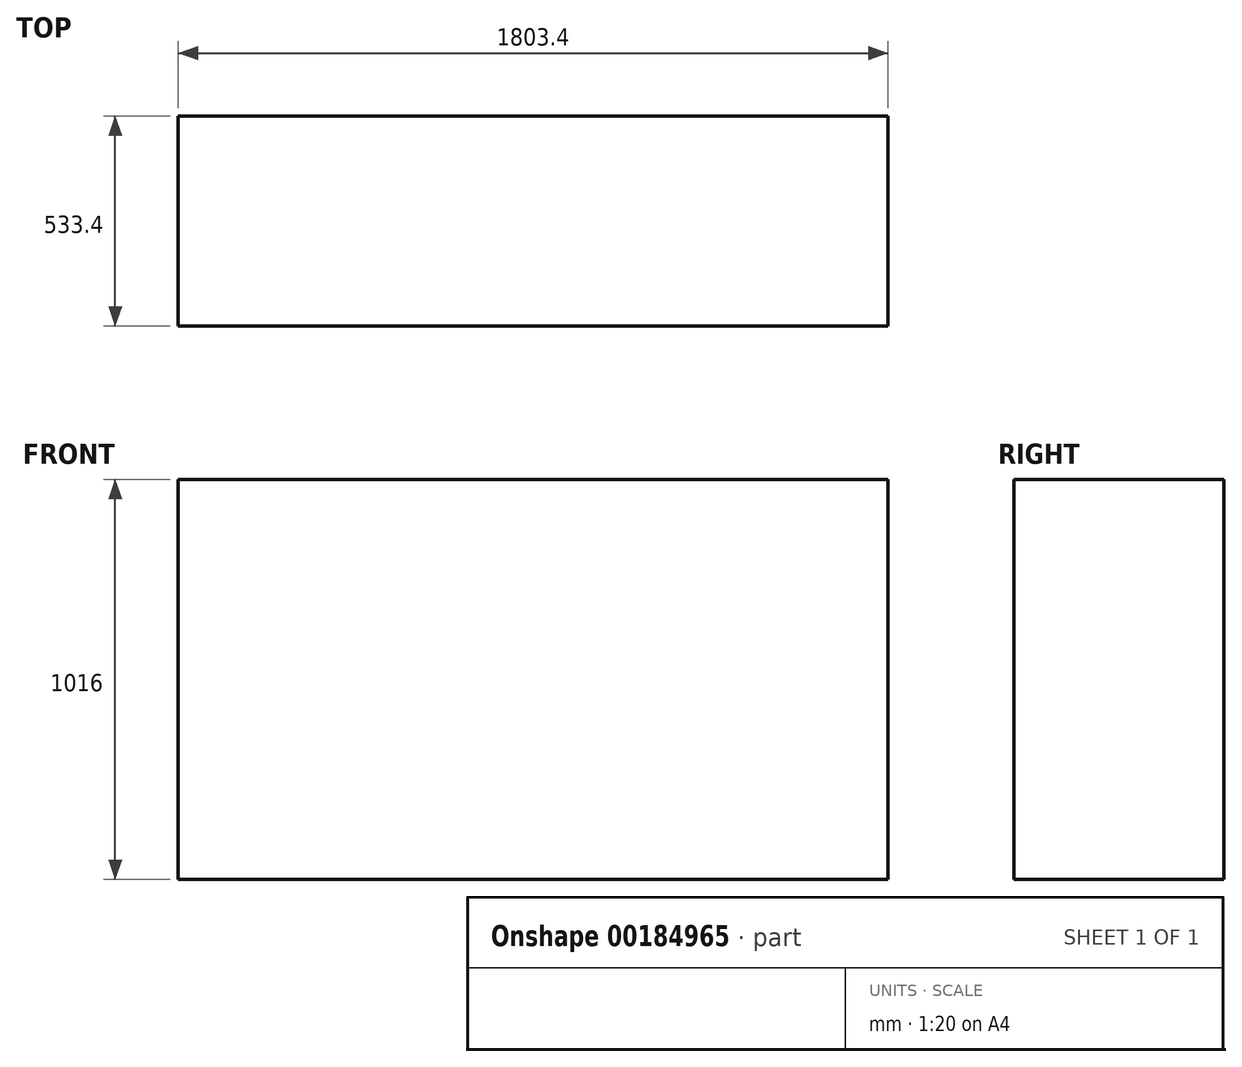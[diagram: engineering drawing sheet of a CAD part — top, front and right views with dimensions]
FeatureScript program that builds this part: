
annotation { "Feature Type Name" : "Feature", "Feature Type Description" : "" }
export const myFeature = defineFeature(function(context is Context, id is Id, definition is map)
    precondition{}
    {
        {
            var Q0;
            Q0=qCreatedBy(makeId("Top.planeOp"),FACE);
            var sketch = newSketch(context, id + "F0", { "sketchPlane" : qUnion([Q0])});
            skLineSegment(sketch, "E0.bottom", {"start": v(901.7, 266.7) * mm, "end": v(-901.7, 266.7) * mm});
            skLineSegment(sketch, "E0.top", {"start": v(901.7, -266.7) * mm, "end": v(-901.7, -266.7) * mm});
            skLineSegment(sketch, "E0.left", {"start": v(901.7, 266.7) * mm, "end": v(901.7, -266.7) * mm});
            skLineSegment(sketch, "E0.right", {"start": v(-901.7, 266.7) * mm, "end": v(-901.7, -266.7) * mm});
            skPoint(sketch, "E0.middle", {"position": v(0, 0) * mm});
            skSolve(sketch);
        }
        {
            var Q0;
            Q0=makeQuery(id+"F0.imprint","IMPRINT",FACE,{"disambiguationData":[TD([[makeQuery(id+"F0.imprint","IMPRINT",EDGE,{"derivedFrom":sQuery(id+"F0.wireOp",EDGE,"E0.bottom")}),1.0]])]});
            extrude(context, id + "F1", {"entities" : qUnion([Q0]), "depth" : 1016 * mm});
        }
    });
